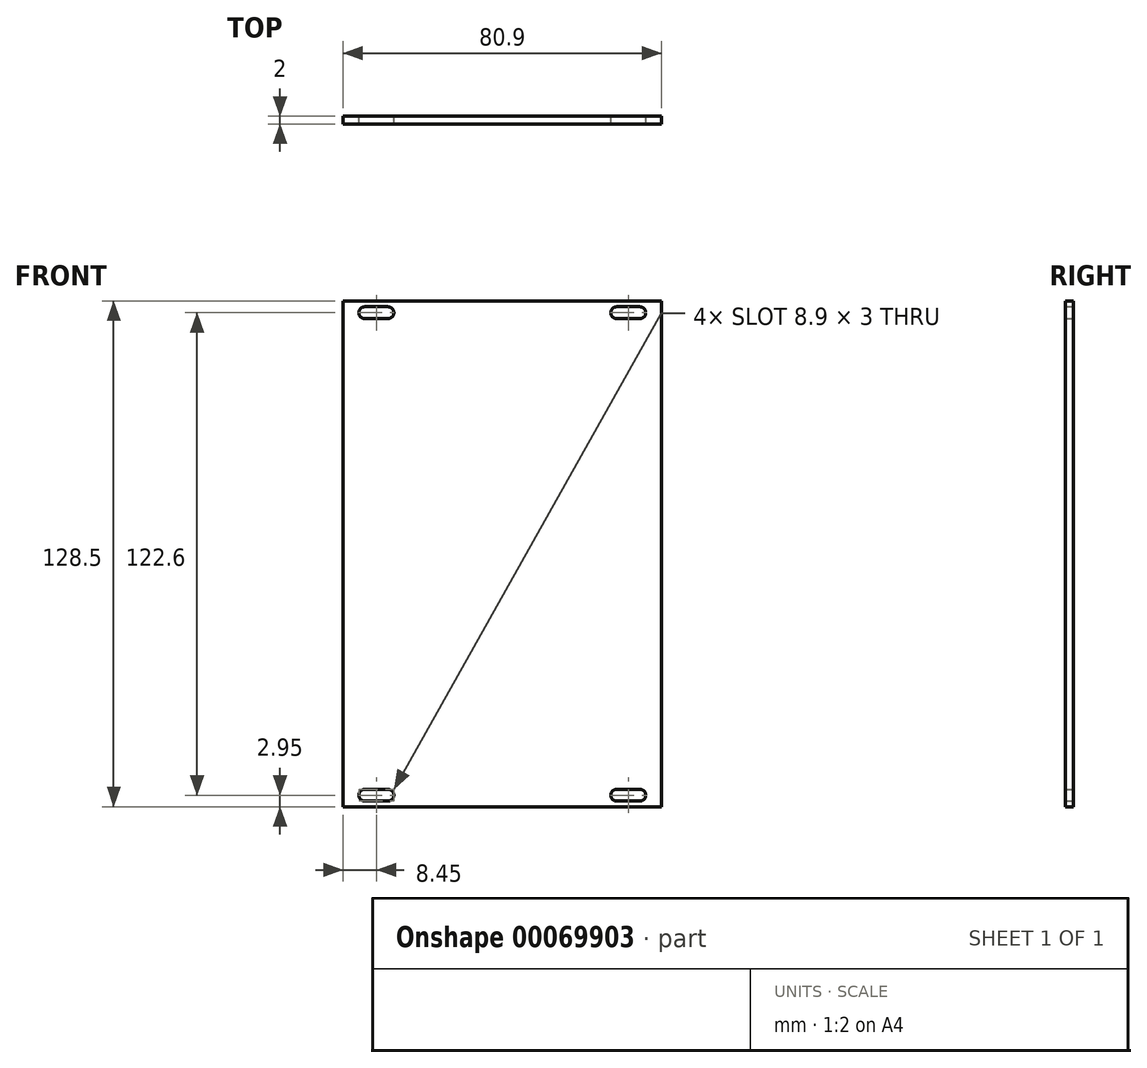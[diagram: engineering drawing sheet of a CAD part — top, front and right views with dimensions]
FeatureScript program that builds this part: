
annotation { "Feature Type Name" : "Feature", "Feature Type Description" : "" }
export const myFeature = defineFeature(function(context is Context, id is Id, definition is map)
    precondition{}
    {
        {
            var Q0;
            Q0=qCreatedBy(makeId("Front.planeOp"),FACE);
            var sketch = newSketch(context, id + "F0", { "sketchPlane" : qUnion([Q0])});
            skLineSegment(sketch, "E0.bottom", {"start": v(40.45, 64.25) * mm, "end": v(-40.45, 64.25) * mm});
            skLineSegment(sketch, "E0.top", {"start": v(40.45, -64.25) * mm, "end": v(-40.45, -64.25) * mm});
            skLineSegment(sketch, "E0.left", {"start": v(40.45, 64.25) * mm, "end": v(40.45, -64.25) * mm});
            skLineSegment(sketch, "E0.right", {"start": v(-40.45, 64.25) * mm, "end": v(-40.45, -64.25) * mm});
            skPoint(sketch, "E0.middle", {"position": v(0, 0) * mm});
            skLineSegment(sketch, "E1", {"start": v(-34.95, 62.8) * mm, "end": v(-29.05, 62.8) * mm});
            skLineSegment(sketch, "E2", {"start": v(-34.95, 59.8) * mm, "end": v(-29.05, 59.8) * mm});
            skArc(sketch, "E3", {"start": v(-29.05, 59.8) * mm, "mid": v(-27.55, 61.3) * mm, "end": v(-29.05, 62.8) * mm});
            skArc(sketch, "E4", {"start": v(-34.95, 62.8) * mm, "mid": v(-36.45, 61.3) * mm, "end": v(-34.95, 59.8) * mm});
            skArc(sketch, "E5.1.0.0", {"start": v(29.05, 62.8) * mm, "mid": v(27.55, 61.3) * mm, "end": v(29.05, 59.8) * mm});
            skLineSegment(sketch, "E5.1.0.1", {"start": v(29.05, 59.8) * mm, "end": v(34.95, 59.8) * mm});
            skLineSegment(sketch, "E5.1.0.2", {"start": v(29.05, 62.8) * mm, "end": v(34.95, 62.8) * mm});
            skArc(sketch, "E5.1.0.3", {"start": v(34.95, 59.8) * mm, "mid": v(36.45, 61.3) * mm, "end": v(34.95, 62.8) * mm});
            skLineSegment(sketch, "E5.direction1", {"start": v(-34.95, 59.8) * mm, "end": v(29.05, 59.8) * mm, "construction": true});
            skLineSegment(sketch, "E6.1.0.0", {"start": v(-34.95, -59.8) * mm, "end": v(-29.05, -59.8) * mm});
            skArc(sketch, "E6.1.0.1", {"start": v(-29.05, -62.8) * mm, "mid": v(-27.55, -61.3) * mm, "end": v(-29.05, -59.8) * mm});
            skLineSegment(sketch, "E6.1.0.2", {"start": v(-34.95, -62.8) * mm, "end": v(-29.05, -62.8) * mm});
            skArc(sketch, "E6.1.0.3", {"start": v(-34.95, -59.8) * mm, "mid": v(-36.45, -61.3) * mm, "end": v(-34.95, -62.8) * mm});
            skLineSegment(sketch, "E6.1.0.4", {"start": v(29.05, -59.8) * mm, "end": v(34.95, -59.8) * mm});
            skArc(sketch, "E6.1.0.5", {"start": v(29.05, -59.8) * mm, "mid": v(27.55, -61.3) * mm, "end": v(29.05, -62.8) * mm});
            skLineSegment(sketch, "E6.1.0.6", {"start": v(29.05, -62.8) * mm, "end": v(34.95, -62.8) * mm});
            skArc(sketch, "E6.1.0.7", {"start": v(34.95, -62.8) * mm, "mid": v(36.45, -61.3) * mm, "end": v(34.95, -59.8) * mm});
            skLineSegment(sketch, "E6.direction1", {"start": v(-34.95, 62.8) * mm, "end": v(-34.95, -59.8) * mm, "construction": true});
            skSolve(sketch);
        }
        {
            var Q0;
            Q0=makeQuery(id+"F0.imprint","IMPRINT",FACE,{"disambiguationData":[TD([[makeQuery(id+"F0.imprint","IMPRINT",EDGE,{"derivedFrom":sQuery(id+"F0.wireOp",EDGE,"E0.bottom")}),1.0]])]});
            extrude(context, id + "F1", {"entities" : qUnion([Q0]), "depth" : 2 * mm});
        }
    });
